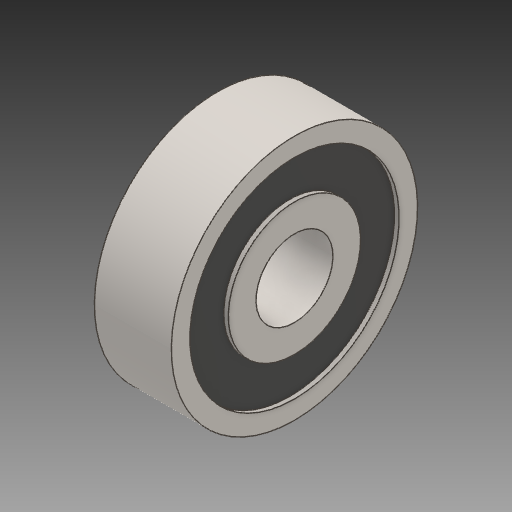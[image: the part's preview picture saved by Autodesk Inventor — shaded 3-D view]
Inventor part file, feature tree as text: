
AUTODESK INVENTOR PART (.ipt)
format: ipt  version: 2017 (Build 210142000, 142)  size: 143,872 bytes
history: mixed  units: mm
features: revolve x1, imported_body x1
ambient origin geometry x8: Origin, YZ Plane, XZ Plane, XY Plane, X Axis, Y Axis, Z Axis, Center Point
bodies: Solid1 (imported_parasolid)
feature tree (2):
  revolve  "Revolve1"  [1 undecoded]
  imported_body  NMx_Import_Brep_tag  [imported B-rep: ~12 faces, bbox_mm=[5.0, 0.0, 5.5]]
note: 1 required parameter value undecoded (feature->parameter linkage not recoverable at this tier; creation-order binding heuristic only, values carry confidence <= 0.55)
